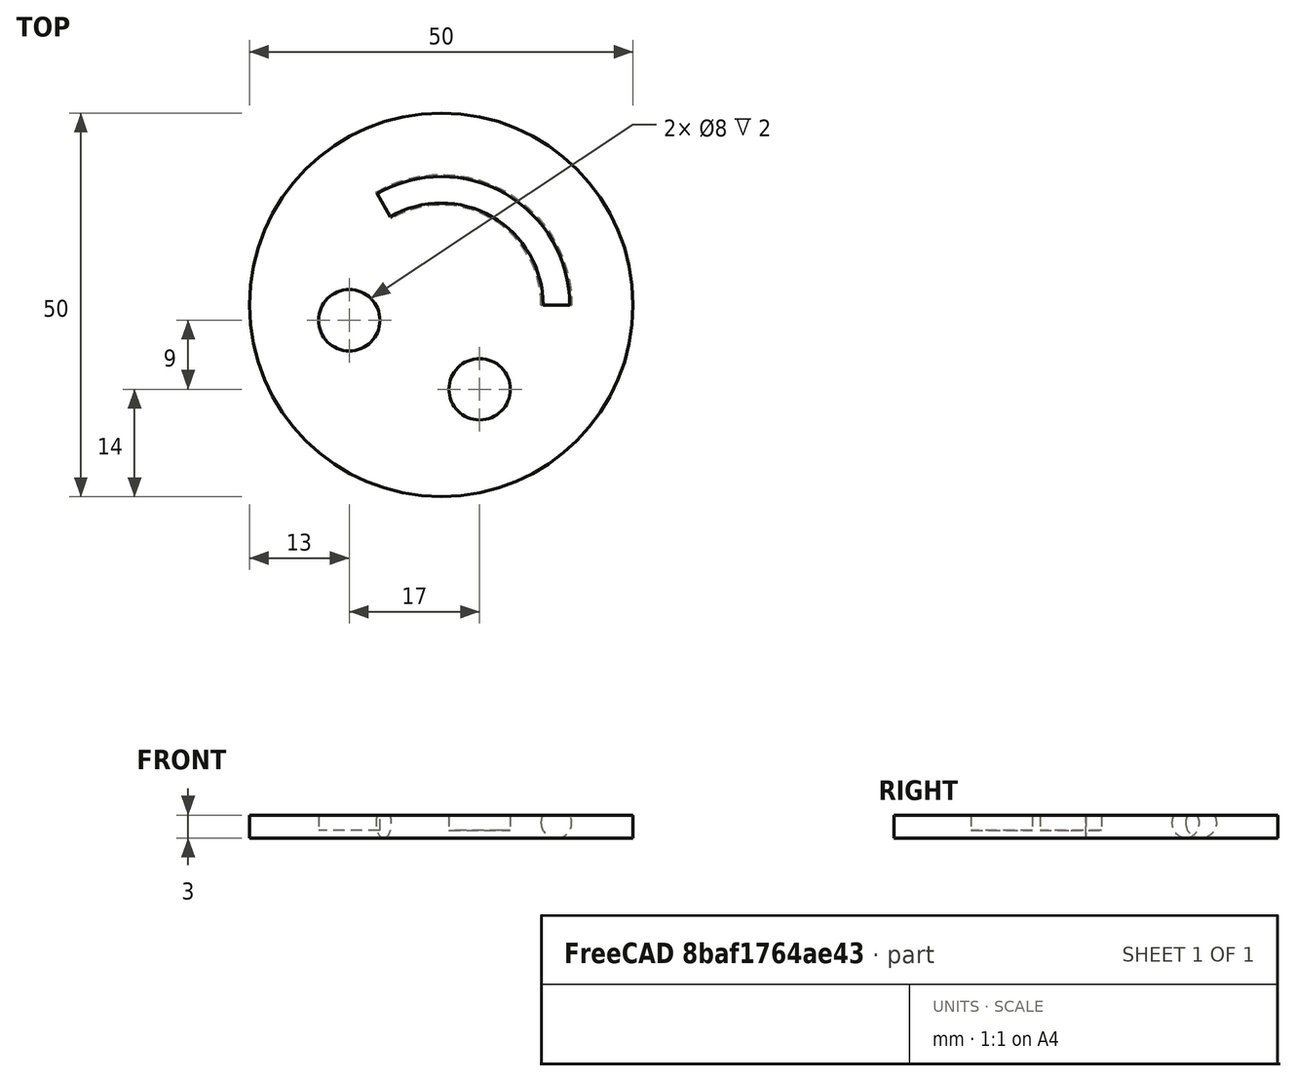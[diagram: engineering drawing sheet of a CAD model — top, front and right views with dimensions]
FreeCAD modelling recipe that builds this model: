
FCSTD DOCUMENT  (FreeCAD 0.21R33694 (Git))
Label: OJT1_T015_somriure
License: All rights reserved
LicenseURL: https://en.wikipedia.org/wiki/All_rights_reserved
objects: Part::Cylinder×3, Part::Cut×3, Part::Torus×1
note: 7 computed .brp shape members not serialized (recipe doc carries the construction recipe); baked Part::Feature solids carry a one-line shape summary decoded from their .brp

FEATURE [Part::Cylinder] Cylinder  label="Cilindre"
  Angle = 360
  AttacherType = Attacher::AttachEngine3D
  FirstAngle = 0
  Height = 3
  Radius = 25
  SecondAngle = 0
FEATURE [Part::Torus] Torus
  Angle1 = -180
  Angle2 = 180
  Angle3 = 120
  AttacherType = Attacher::AttachEngine3D
  Placement = pos=(0,0,2) rot=(0,0,1;0rad)
  Radius1 = 15
  Radius2 = 2
FEATURE [Part::Cut] Cut
  Base = -> Cylinder
  Tool = -> Torus
FEATURE [Part::Cylinder] Cylinder001  label="Cilindre001"
  Angle = 360
  AttacherType = Attacher::AttachEngine3D
  FirstAngle = 0
  Height = 4
  Placement = pos=(5,-11,1) rot=(0,0,1;0.785398rad)
  Radius = 4
  SecondAngle = 0
  expr: .Placement.Rotation.Yaw = 45
FEATURE [Part::Cylinder] Cylinder002  label="Cilindre002"
  Angle = 360
  AttacherType = Attacher::AttachEngine3D
  FirstAngle = 0
  Height = 10
  Placement = pos=(-12,-2,1) rot=(0,0,1;0rad)
  Radius = 4
  SecondAngle = 0
  expr: .Placement.Base.y = -2
FEATURE [Part::Cut] Cut001
  Base = -> Cut
  Tool = -> Cylinder002
FEATURE [Part::Cut] Cut002
  Base = -> Cut001
  Tool = -> Cylinder001
